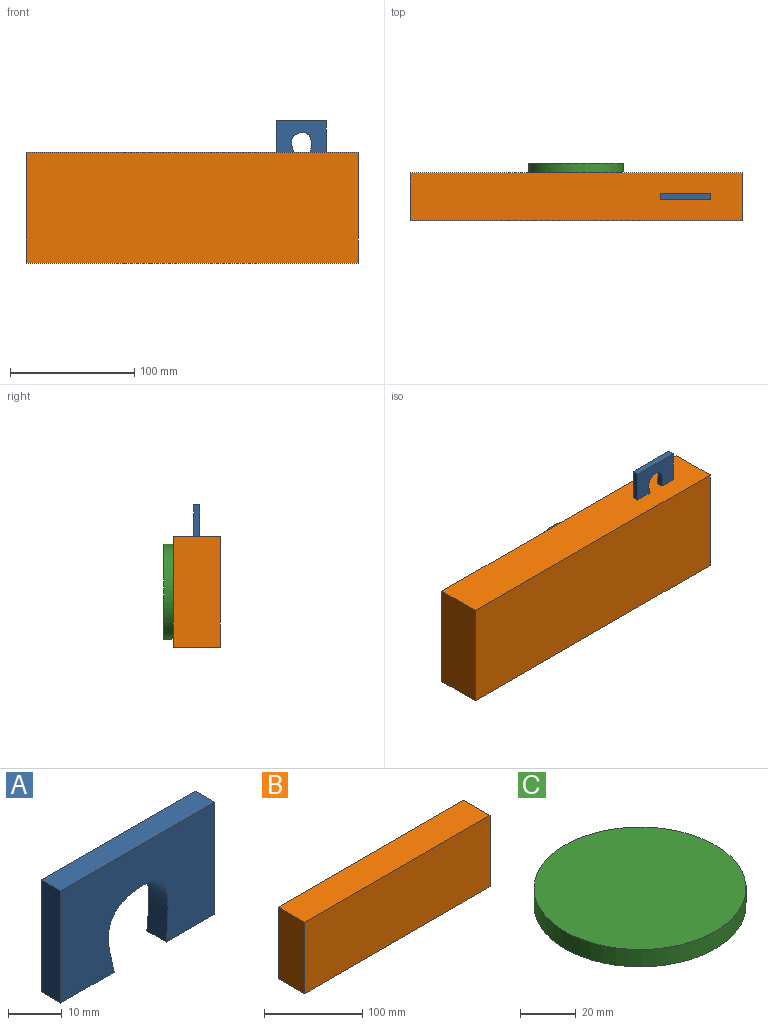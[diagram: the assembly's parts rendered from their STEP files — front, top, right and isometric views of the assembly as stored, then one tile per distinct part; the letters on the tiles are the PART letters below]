
ASSEMBLY  parts=3 mates=2
PART A: 8 faces, bbox 40.4x5.1x25.4 mm
  f0: plane 25.4x5.08mm, normal (-1,0,0), area 129mm2, adj f1,f5,f6,f7
  f1: plane 14.04x5.08mm, normal (0,0,-1), area 71.3mm2, adj f0,f2,f6,f7
  f2: extruded ~15.94x15.64mm, area 211.7mm2, adj f1,f3,f6,f7
  f3: plane 12.7x5.08mm, normal (0,0,-1), area 64.5mm2, adj f2,f4,f6,f7
  f4: plane 25.4x5.08mm, normal (1,0,0), area 129mm2, adj f3,f5,f6,f7
  f5: plane 40.37x5.08mm, normal (0,0,1), area 205.1mm2, adj f0,f4,f6,f7
  f6: plane 40.37x25.4mm, normal (0,-1,0), area 804.1mm2, adj f0,f1,f2,f3,f4,f5
  f7: plane 40.37x25.4mm, normal (0,1,0), area 804.1mm2, adj f0,f1,f2,f3,f4,f5
PART B: 6 faces, bbox 266.7x38.1x88.9 mm
  f0: plane 266.7x38.1mm, normal (0,0,1), area 10161.3mm2, adj f1,f3,f4,f5
  f1: plane 88.9x38.1mm, normal (-1,0,0), area 3387.1mm2, adj f0,f2,f4,f5
  f2: plane 266.7x38.1mm, normal (0,0,-1), area 10161.3mm2, adj f1,f3,f4,f5
  f3: plane 88.9x38.1mm, normal (1,0,0), area 3387.1mm2, adj f0,f2,f4,f5
  f4: plane 266.7x88.9mm, normal (0,-1,0), area 23709.6mm2, adj f0,f1,f2,f3
  f5: plane 266.7x88.9mm, normal (0,1,0), area 23709.6mm2, adj f0,f1,f2,f3
PART C: 3 faces, bbox 76.2x76.2x7.6 mm
  f0: cylinder r=38.1mm len=76.2mm, axis (0,0,-1), area 1824.1mm2, adj f1,f2
  f1: plane 76.2x76.2mm, normal (0,0,1), area 4560.4mm2, adj f0
  f2: plane 76.2x76.2mm, normal (0,0,-1), area 4560.4mm2, adj f0
PLACE A t=(258.01,-10.44,130.76)mm
PLACE B t=(-19.14,6.07,13.19)mm fixed
PLACE C rot(axis=(0.58,0.58,-0.58),120deg) t=(77.77,13.69,156.44)mm
MATE fastened B.f0 <-> A.f3  axis (0,0,1) through (281.46,-12.98,142.27)mm
MATE fastened C.f0 <-> B.f5  axis (0,-1,0) through (148.11,6.07,97.82)mm
